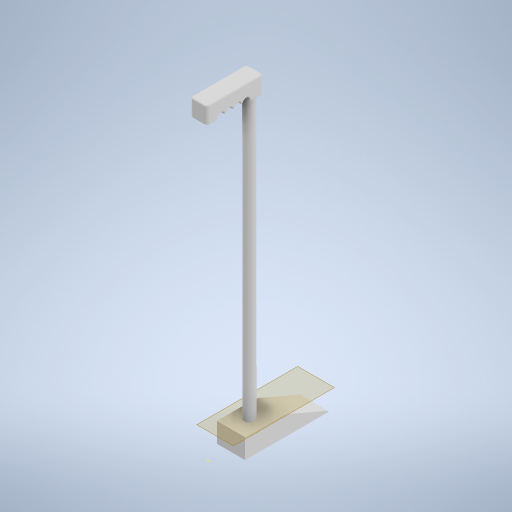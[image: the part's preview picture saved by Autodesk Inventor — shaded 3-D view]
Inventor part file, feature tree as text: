
AUTODESK INVENTOR PART (.ipt)
format: ipt  version: 2023.1 (Build 271208000, 208)  size: 389,632 bytes
history: native  units: mm
features: sketch x10, extrude x6, fillet x4, plane x1, pattern_linear x1
ambient origin geometry x8: Origin, YZ Plane, XZ Plane, XY Plane, X Axis, Y Axis, Z Axis, Center Point
bodies: Solid1 (feature_tree), Solid2 (feature_tree), Solid3 (feature_tree)
feature tree (22):
  extrude  "Stoppningen"  Depth=2.0mm TaperAngle=0.0deg
  extrude  "Underlägningen"  Depth=70.0mm
  fillet  "Fillet1"  Radius=50.0mm
  sketch  "Sketch10"  dims[d40=90.0mm d41=5.0mm]
  plane  "Work Plane1"
  extrude  "Pinnen"  Depth=2.0mm
  extrude  "Handtaget"  Depth=25.0mm
  fillet  "Fillet2"  Radius=500.0mm
  fillet  "Fillet8"  Radius=18.0mm
  pattern_linear  "Rectangular Pattern2"  Count1=3 Spacing1=0.0mm
  fillet  "Fillet9"  Radius=100.0mm
  sketch  "Sketch14"  dims[d60=12.0mm d61=6.0mm d62=4.0mm d63=2.0mm d64=90.0deg d65=8.0mm d66=20.594885mm]
  extrude  "Extrusion2"  Depth=15.0mm
  sketch  "Sketch4"  dims[d16=35.0mm d17=70.0mm d18=50.0mm d19=0.0mm]
  extrude  "Extrusion1"  Depth=5.0mm
  sketch  "Sketch3"  dims[d0=2.0mm d1=0.0mm d2=2.0mm d3=0.0mm]
  sketch  "Sketch5"  dims[d20=77.0mm d21=2.0mm]
  sketch  "Sketch8"  dims[d22=50.0mm d23=0.0mm d24=25.0mm d28=500.0mm d29=0.0mm d30=18.0mm d31=30.0mm d32=0.0mm d33=100.0mm]
  sketch  "Sketch9"  dims[d38=15.0mm d39=15.0mm]
  sketch  "Sketch11"  dims[d58=2.0mm]
  sketch  "Sketch12"  dims[d59=20.0mm]
  sketch  "Sketch15"  dims[d67=40.0mm d69=15.0mm d70=2.0mm d4=0.5mm d5=0.872665mm d6=0.5mm d7=0.872665mm d8=0.5mm d9=0.872665mm d11=0.5mm d12=0.872665mm d13=0.5mm d14=0.872665mm d25=0.872665mm d34=0.872665mm]
